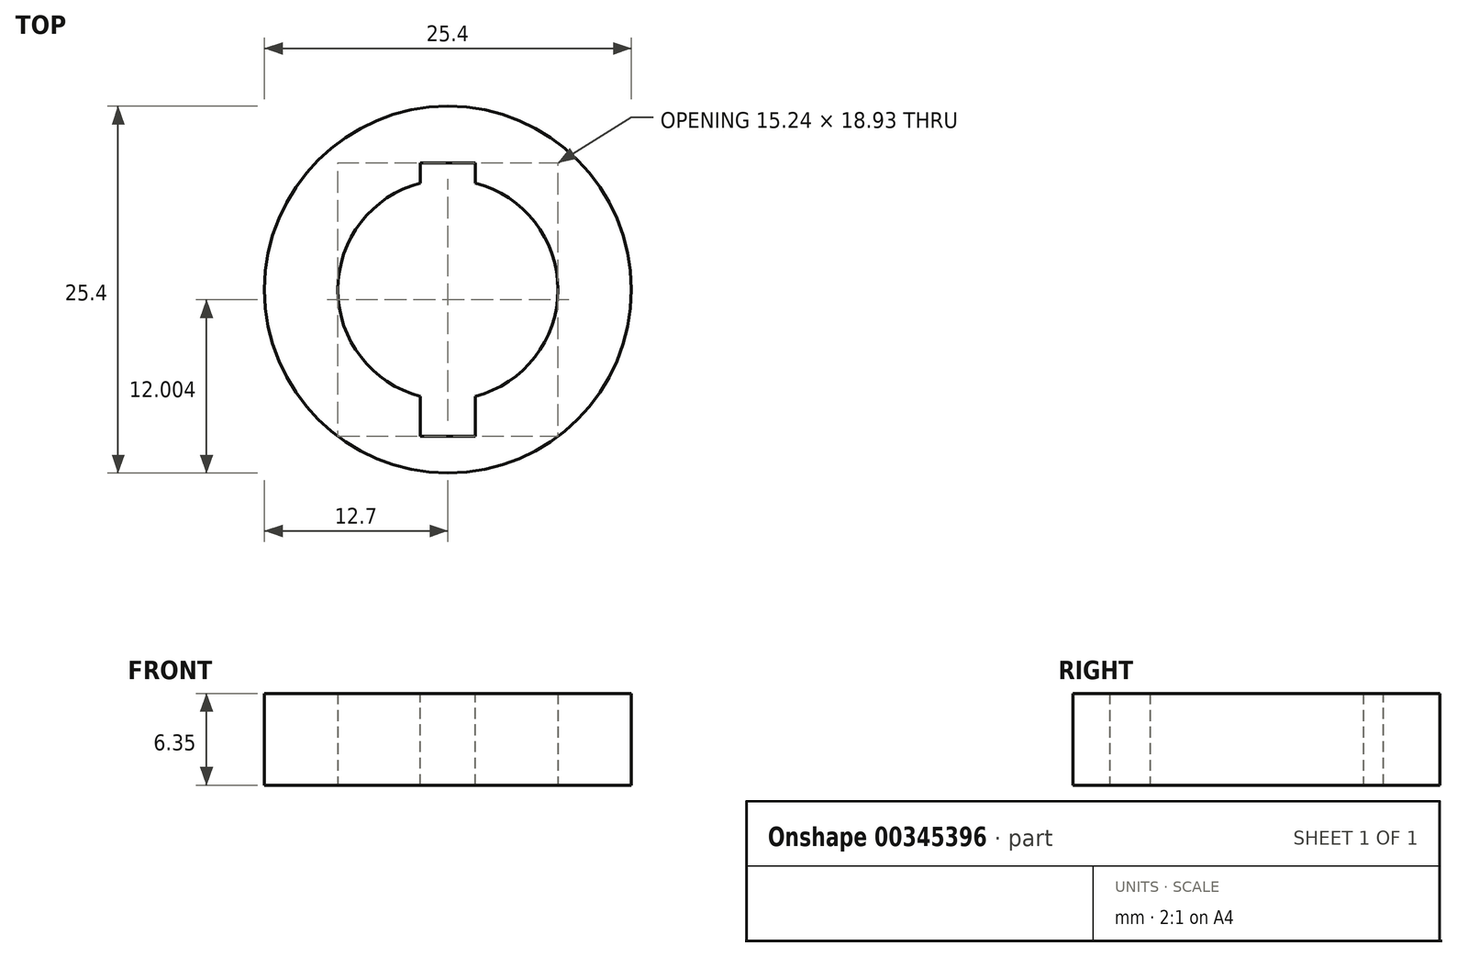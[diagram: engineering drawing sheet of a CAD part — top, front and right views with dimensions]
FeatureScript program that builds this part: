
annotation { "Feature Type Name" : "Feature", "Feature Type Description" : "" }
export const myFeature = defineFeature(function(context is Context, id is Id, definition is map)
    precondition{}
    {
        {
            var Q0;
            Q0=qCreatedBy(makeId("Top.planeOp"),FACE);
            var sketch = newSketch(context, id + "F0", { "sketchPlane" : qUnion([Q0])});
            skCircle(sketch, "E0", {"center": v(0, 0) * mm, "radius": 12.7 * mm});
            skCircle(sketch, "E1", {"center": v(0, 0) * mm, "radius": 7.62 * mm});
            skLineSegment(sketch, "E2.bottom", {"start": v(-1.9, 10.16) * mm, "end": v(1.9, 10.16) * mm});
            skLineSegment(sketch, "E2.top", {"start": v(-1.9, -10.16) * mm, "end": v(1.9, -10.16) * mm});
            skLineSegment(sketch, "E2.left", {"start": v(-1.9, 10.16) * mm, "end": v(-1.9, -10.16) * mm});
            skLineSegment(sketch, "E2.right", {"start": v(1.9, 10.16) * mm, "end": v(1.9, -10.16) * mm});
            skSolve(sketch);
        }
        {
            var Q0;
            Q0=makeQuery(id+"F0.imprint","IMPRINT",FACE,{"disambiguationData":[TD([[makeQuery(id+"F0.imprint","IMPRINT",EDGE,{"derivedFrom":sQuery(id+"F0.wireOp",EDGE,"E0")}),1.0]])]});
            extrude(context, id + "F1", {"entities" : qUnion([Q0]), "depth" : 6.35 * mm});
        }
        {
            var Q0;
            Q0=makeQuery(id+"F1.opExtrude","CAP_FACE",FACE,{"disambiguationData":[OSD([sQuery(id+"F0.wireOp",EDGE,"E0"),sQuery(id+"F0.wireOp",EDGE,"E1"),sQuery(id+"F0.wireOp",EDGE,"E2.bottom"),sQuery(id+"F0.wireOp",EDGE,"E2.top"),sQuery(id+"F0.wireOp",EDGE,"E2.left"),sQuery(id+"F0.wireOp",EDGE,"E2.right")])],"isStart":false});
            var sketch = newSketch(context, id + "F2", { "sketchPlane" : qUnion([Q0])});
            skLineSegment(sketch, "E3", {"start": v(-1.9, 10.16) * mm, "end": v(-1.9, 8.77) * mm});
            skLineSegment(sketch, "E4", {"start": v(1.9, 10.16) * mm, "end": v(1.9, 8.77) * mm});
            skLineSegment(sketch, "E5", {"start": v(1.9, 8.77) * mm, "end": v(-1.9, 8.77) * mm});
            skLineSegment(sketch, "E6", {"start": v(-1.9, 10.16) * mm, "end": v(1.9, 10.16) * mm});
            skSolve(sketch);
        }
        {
            var Q0;
            Q0 = qSketchRegion(id + "F2", true);
            extrude(context, id + "F3", {"entities" : qUnion([Q0]), "operationType" : NewBodyOperationType.ADD, "oppositeDirection" : true, "depth" : 6.35 * mm});
        }
    });
